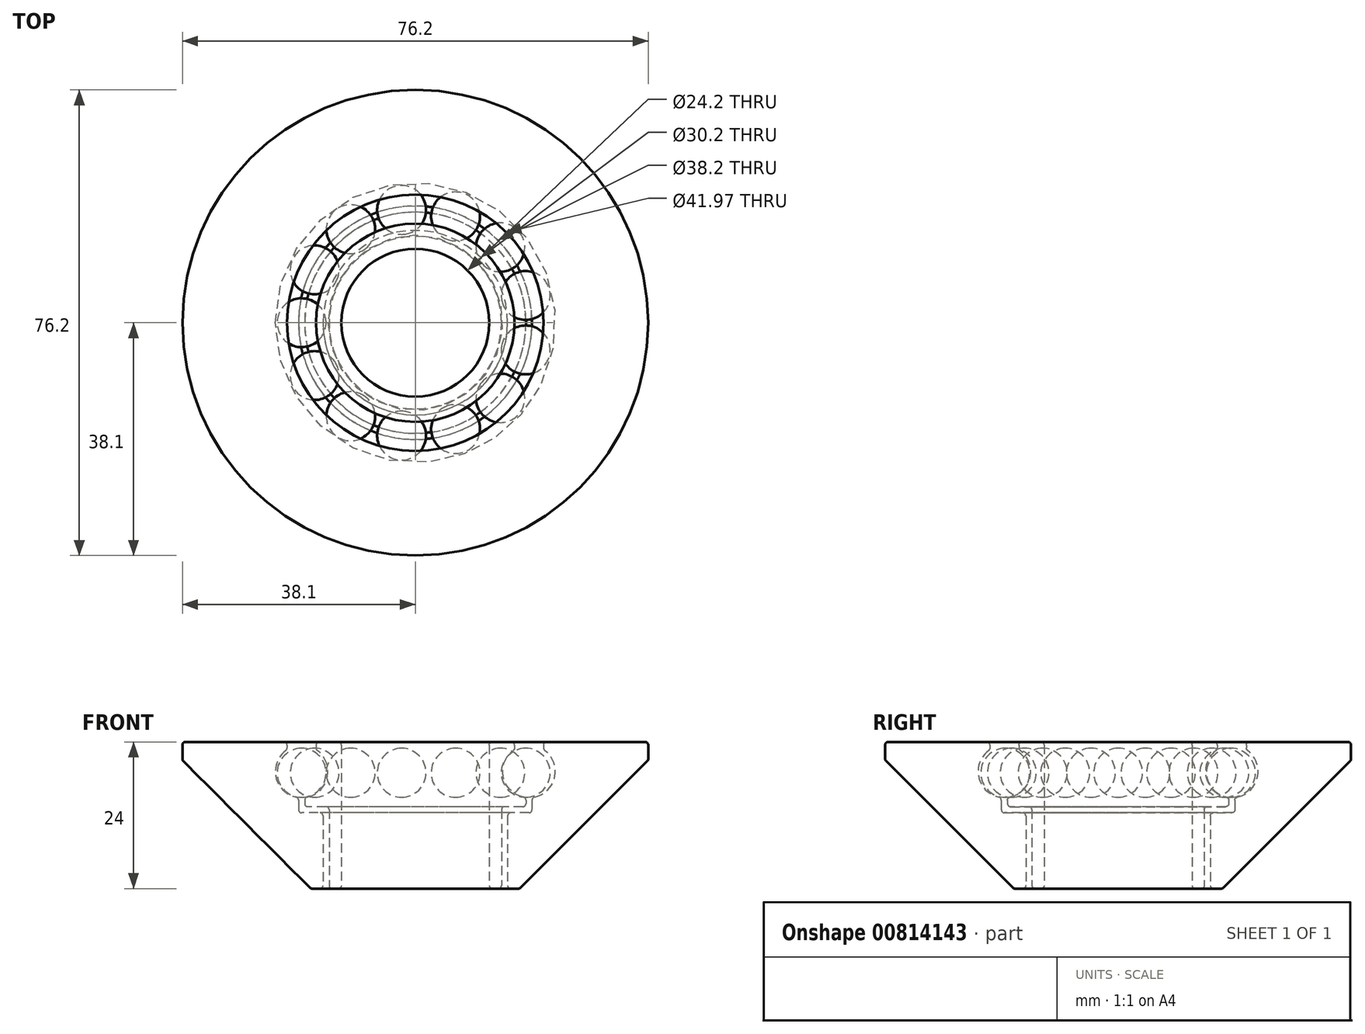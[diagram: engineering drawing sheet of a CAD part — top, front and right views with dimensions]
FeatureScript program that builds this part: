
annotation { "Feature Type Name" : "Feature", "Feature Type Description" : "" }
export const myFeature = defineFeature(function(context is Context, id is Id, definition is map)
    precondition{}
    {
        {
            var Q0;
            Q0=qCreatedBy(makeId("Front.planeOp"),FACE);
            var sketch = newSketch(context, id + "F0", { "sketchPlane" : qUnion([Q0])});
            skLineSegment(sketch, "E0", {"start": v(0, -18.14) * mm, "end": v(0, 38.96) * mm, "construction": true});
            skLineSegment(sketch, "E1", {"start": v(-12.1, 0) * mm, "end": v(-12.1, 24) * mm});
            skLineSegment(sketch, "E2", {"start": v(-12.1, 24) * mm, "end": v(-16.22, 24) * mm});
            skLineSegment(sketch, "E3", {"start": v(-18.1, 24) * mm, "end": v(-18.1, 23.14) * mm, "construction": true});
            skLineSegment(sketch, "E4", {"start": v(-18.1, 13.4) * mm, "end": v(-14.1, 13.4) * mm});
            skLineSegment(sketch, "E5", {"start": v(-14.1, 13.4) * mm, "end": v(-14.1, 0) * mm});
            skLineSegment(sketch, "E6", {"start": v(-14.1, 0) * mm, "end": v(-12.1, 0) * mm});
            skLineSegment(sketch, "E7", {"start": v(-15.1, 12.4) * mm, "end": v(-15.1, 0) * mm});
            skLineSegment(sketch, "E8", {"start": v(-15.1, 0) * mm, "end": v(-17.1, 0) * mm});
            skLineSegment(sketch, "E9", {"start": v(-17.1, 0) * mm, "end": v(-38.1, 21) * mm});
            skLineSegment(sketch, "E10", {"start": v(-38.1, 21) * mm, "end": v(-38.1, 24) * mm});
            skLineSegment(sketch, "E11", {"start": v(-38.1, 24) * mm, "end": v(-20.98, 24) * mm});
            skLineSegment(sketch, "E12", {"start": v(-19.1, 24) * mm, "end": v(-19.1, 23.14) * mm, "construction": true});
            skLineSegment(sketch, "E13", {"start": v(-19.1, 12.4) * mm, "end": v(-15.1, 12.4) * mm});
            skCircle(sketch, "E14", {"center": v(-18.6, 19.17) * mm, "radius": 4 * mm, "construction": true});
            skArc(sketch, "E15", {"start": v(-18.1, 14.9) * mm, "mid": v(-14.42, 18.17) * mm, "end": v(-16.22, 22.75) * mm});
            skLineSegment(sketch, "E16.trimOffspring", {"start": v(-18.1, 14.9) * mm, "end": v(-18.1, 13.4) * mm});
            skLineSegment(sketch, "E17.trimOffspring", {"start": v(-19.1, 14.9) * mm, "end": v(-19.1, 12.4) * mm});
            skArc(sketch, "E18.trimOffspring", {"start": v(-20.98, 22.75) * mm, "mid": v(-22.78, 18.17) * mm, "end": v(-19.1, 14.9) * mm});
            skLineSegment(sketch, "E19", {"start": v(-16.22, 24) * mm, "end": v(-16.22, 22.75) * mm});
            skLineSegment(sketch, "E20", {"start": v(-20.98, 24) * mm, "end": v(-20.98, 22.75) * mm});
            skSolve(sketch);
        }
        {
            var Q0;
            Q0=makeQuery(id+"F0.imprint","IMPRINT",FACE,{"disambiguationData":[TD([[makeQuery(id+"F0.imprint","IMPRINT",EDGE,{"derivedFrom":sQuery(id+"F0.wireOp",EDGE,"E7")}),-1.0]])]});
            var Q1;
            Q1=makeQuery(id+"F0.imprint","IMPRINT",FACE,{"disambiguationData":[TD([[makeQuery(id+"F0.imprint","IMPRINT",EDGE,{"derivedFrom":sQuery(id+"F0.wireOp",EDGE,"E1")}),1.0]])]});
            var Q2;
            Q2=sQuery(id+"F0.wireOp",EDGE,"E0");
            revolve(context, id + "F1", {"surfaceOperationType" : NewSurfaceOperationType.NEW, "entities" : qUnion([Q0, Q1]), "axis" : qUnion([Q2]), "revolveType" : RevolveType.FULL});
        }
        {
            var Q0;
            Q0=qCreatedBy(makeId("Front.planeOp"),FACE);
            var sketch = newSketch(context, id + "F2", { "sketchPlane" : qUnion([Q0])});
            skLineSegment(sketch, "E21", {"start": v(-18.6, 22.95) * mm, "end": v(-18.6, 14.95) * mm});
            skArc(sketch, "E22", {"start": v(-18.6, 14.95) * mm, "mid": v(-22.6, 18.95) * mm, "end": v(-18.6, 22.95) * mm});
            skLineSegment(sketch, "E23", {"start": v(0, -2.75) * mm, "end": v(0, 27.7) * mm, "construction": true});
            skSolve(sketch);
        }
        {
            var Q0;
            Q0=qSketchRegion(id+"F2",true);
            var Q1;
            Q1=sQuery(id+"F2.wireOp",EDGE,"E21");
            revolve(context, id + "F3", {"surfaceOperationType" : NewSurfaceOperationType.NEW, "entities" : qUnion([Q0]), "axis" : qUnion([Q1]), "revolveType" : RevolveType.FULL});
        }
        {
            var Q0;
            Q0=makeQuery(id+"F3.opRevolve","SWEPT_BODY",BODY,{"disambiguationData":[OSD([sQuery(id+"F2.wireOp",EDGE,"E21"),sQuery(id+"F2.wireOp",EDGE,"E22")])]});
            var Q1;
            Q1=sQuery(id+"F0.wireOp",EDGE,"E0");
            circularPattern(context, id + "F4", {"entities" : qUnion([Q0]), "axis" : qUnion([Q1]), "angle" : 360 * degree, "instanceCount" : 13, "equalSpace" : true});
        }
        {
            var Q0;
            Q0=makeQuery(id+"F1.opRevolve","SWEPT_FACE",FACE,{"disambiguationData":[OSD([sQuery(id+"F0.wireOp",EDGE,"E11")])]});
            var Q1;
            Q1=makeQuery(id+"F1.opRevolve","SWEPT_FACE",FACE,{"disambiguationData":[OSD([sQuery(id+"F0.wireOp",EDGE,"E9")])]});
            var Q2;
            Q2=makeQuery(id+"F1.opRevolve","SWEPT_FACE",FACE,{"disambiguationData":[OSD([sQuery(id+"F0.wireOp",EDGE,"E6")])]});
            var Q3;
            Q3=makeQuery(id+"F1.opRevolve","SWEPT_EDGE",EDGE,{"disambiguationData":[OSD([sQuery(id+"F0.wireOp",EDGE,"E7"),sQuery(id+"F0.wireOp",EDGE,"E8")])]});
            var Q4;
            Q4=makeQuery(id+"F1.opRevolve","SWEPT_FACE",FACE,{"disambiguationData":[OSD([sQuery(id+"F0.wireOp",EDGE,"E2")])]});
            var Q5;
            Q5=makeQuery(id+"F1.opRevolve","SWEPT_EDGE",EDGE,{"disambiguationData":[OSD([sQuery(id+"F0.wireOp",EDGE,"E15"),sQuery(id+"F0.wireOp",EDGE,"E19")])]});
            var Q6;
            Q6=makeQuery(id+"F1.opRevolve","SWEPT_EDGE",EDGE,{"disambiguationData":[OSD([sQuery(id+"F0.wireOp",EDGE,"E18.trimOffspring"),sQuery(id+"F0.wireOp",EDGE,"E20")])]});
            var Q7;
            Q7=makeQuery(id+"F1.opRevolve","SWEPT_FACE",FACE,{"disambiguationData":[OSD([sQuery(id+"F0.wireOp",EDGE,"E16.trimOffspring")])]});
            var Q8;
            Q8=makeQuery(id+"F1.opRevolve","SWEPT_EDGE",EDGE,{"disambiguationData":[OSD([sQuery(id+"F0.wireOp",EDGE,"E4"),sQuery(id+"F0.wireOp",EDGE,"E5")])]});
            var Q9;
            Q9=makeQuery(id+"F1.opRevolve","SWEPT_EDGE",EDGE,{"disambiguationData":[OSD([sQuery(id+"F0.wireOp",EDGE,"E7"),sQuery(id+"F0.wireOp",EDGE,"E13")])]});
            var Q10;
            Q10=makeQuery(id+"F1.opRevolve","SWEPT_FACE",FACE,{"disambiguationData":[OSD([sQuery(id+"F0.wireOp",EDGE,"E17.trimOffspring")])]});
            fillet(context, id + "F5", {"entities" : qUnion([Q0, Q1, Q2, Q3, Q4, Q5, Q6, Q7, Q8, Q9, Q10]), "radius" : .5 * mm, "tangentPropagation" : true, "allowEdgeOverflow" : false});
        }
    });
